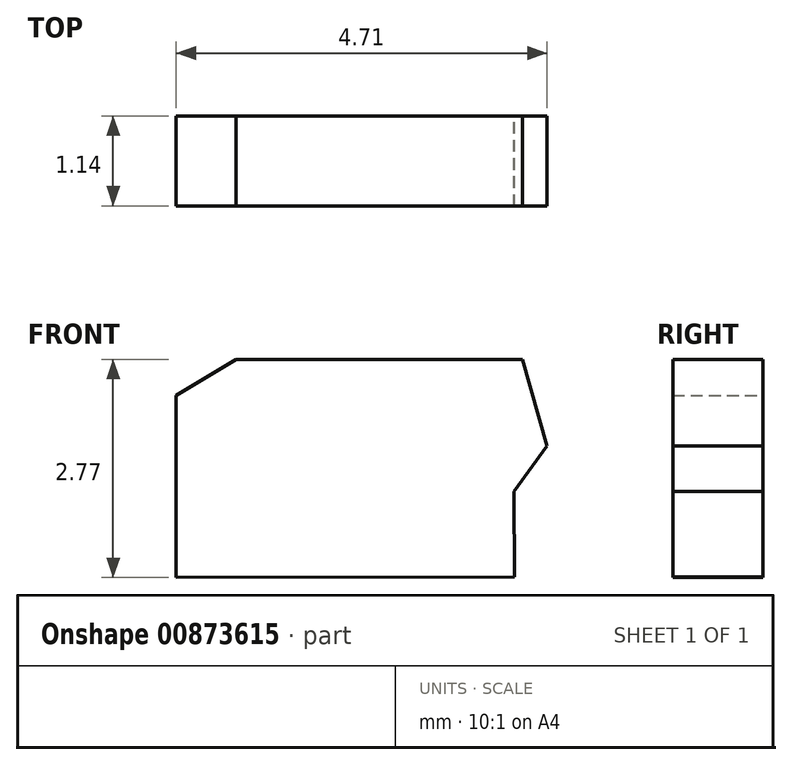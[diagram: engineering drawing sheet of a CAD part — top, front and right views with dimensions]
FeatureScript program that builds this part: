
annotation { "Feature Type Name" : "Feature", "Feature Type Description" : "" }
export const myFeature = defineFeature(function(context is Context, id is Id, definition is map)
    precondition{}
    {
        {
            var Q0;
            Q0=qCreatedBy(makeId("Front.planeOp"),FACE);
            var sketch = newSketch(context, id + "F0", { "sketchPlane" : qUnion([Q0])});
            skLineSegment(sketch, "E0", {"start": v(-67.67, -1.14) * mm, "end": v(-67.67, -1.14) * mm});
            skArc(sketch, "E1", {"start": v(-3.73, 8.14) * mm, "mid": v(1.74, 5.8) * mm, "end": v(7.42, 4.04) * mm});
            skLineSegment(sketch, "E2", {"start": v(7.42, 4.04) * mm, "end": v(116.1, 0) * mm});
            skLineSegment(sketch, "E3", {"start": v(-69.08, -1.14) * mm, "end": v(116, -0.88) * mm});
            skPoint(sketch, "E3.startSnap0", {"position": v(-67.67, -1.14) * mm});
            skPoint(sketch, "E3.startSnap1", {"position": v(-69.08, -5.06) * mm});
            skLineSegment(sketch, "E4", {"start": v(116, -0.88) * mm, "end": v(-69.08, -1.14) * mm});
            skLineSegment(sketch, "E5", {"start": v(-71.64, -1.14) * mm, "end": v(-69.08, -1.14) * mm});
            skLineSegment(sketch, "E6", {"start": v(-25.66, 0) * mm, "end": v(-25.66, -1.08) * mm});
            skLineSegment(sketch, "E7", {"start": v(-6.34, -0.88) * mm, "end": v(-5.24, -1.05) * mm});
            skLineSegment(sketch, "E8", {"start": v(116, -0.88) * mm, "end": v(117.89, -0.88) * mm});
            skLineSegment(sketch, "E9", {"start": v(116.1, 0) * mm, "end": v(117.89, -0.88) * mm});
            skPoint(sketch, "E10.orphan", {"position": v(-36.88, -4.46) * mm});
            skPoint(sketch, "E11.end.orphan", {"position": v(-40.75, -4.46) * mm});
            skPoint(sketch, "E12.start.orphan", {"position": v(-64.86, -4.46) * mm});
            skPoint(sketch, "E13.orphan", {"position": v(-67.67, -4.46) * mm});
            skPoint(sketch, "E14.orphan", {"position": v(-70.49, -5.66) * mm});
            skPoint(sketch, "E15.orphan", {"position": v(-25.6, 0.84) * mm});
            skPoint(sketch, "E16.start.orphan", {"position": v(-21.42, 0) * mm});
            skPoint(sketch, "E17.orphan", {"position": v(-25.55, 1.68) * mm});
            skPoint(sketch, "E18.start.orphan", {"position": v(-30.28, 0) * mm});
            skPoint(sketch, "E19.end.orphan", {"position": v(-15.31, 4.04) * mm});
            skPoint(sketch, "E20.end.orphan", {"position": v(-27.06, 7.6) * mm});
            skPoint(sketch, "E21.end.orphan", {"position": v(-30.34, 7.6) * mm});
            skPoint(sketch, "E22.end.orphan", {"position": v(-36.88, 13.49) * mm});
            skPoint(sketch, "E23.end.orphan", {"position": v(-36.88, 1.47) * mm});
            skPoint(sketch, "E24.start.orphan", {"position": v(-40.75, 2.17) * mm});
            skPoint(sketch, "E25.start.orphan", {"position": v(-64.86, 2.17) * mm});
            skPoint(sketch, "E26.start.orphan", {"position": v(-67.67, 2.17) * mm});
            skPoint(sketch, "E27.start.orphan", {"position": v(-70.49, 4.58) * mm});
            skPoint(sketch, "E28.start.orphan", {"position": v(-23.51, 0.42) * mm});
            skPoint(sketch, "E29.start.orphan", {"position": v(-21.42, 3.91) * mm});
            skPoint(sketch, "E30.start.orphan", {"position": v(-19, 2.1) * mm});
            skPoint(sketch, "E31.start.orphan", {"position": v(-13.33, 2.1) * mm});
            skPoint(sketch, "E32.start.orphan", {"position": v(-22.63, -0.44) * mm});
            skPoint(sketch, "E33.start.orphan", {"position": v(-21.84, 0) * mm});
            skPoint(sketch, "E34.start.orphan", {"position": v(-21.6, -0.44) * mm});
            skLineSegment(sketch, "E35", {"start": v(-25.66, 0) * mm, "end": v(-25.24, 0.58) * mm});
            skLineSegment(sketch, "E36", {"start": v(-25.24, 0.58) * mm, "end": v(-25.55, 1.68) * mm});
            skLineSegment(sketch, "E37", {"start": v(-29.2, 1.68) * mm, "end": v(-25.55, 1.68) * mm});
            skLineSegment(sketch, "E38", {"start": v(-29.2, 1.68) * mm, "end": v(-29.95, 1.22) * mm});
            skLineSegment(sketch, "E39", {"start": v(-29.95, 1.22) * mm, "end": v(-29.95, -1.09) * mm});
            skSolve(sketch);
        }
        {
            var Q0;
            Q0 = qSketchRegion(id + "F0", true);
            extrude(context, id + "F1", {"entities" : qUnion([Q0]), "depth" : 1.14 * mm, "offsetDistance" : 25.4 * mm});
        }
    });
